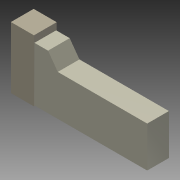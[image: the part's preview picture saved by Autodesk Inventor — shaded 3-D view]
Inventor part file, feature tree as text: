
AUTODESK INVENTOR PART (.ipt)
format: ipt  version: 2011 (Build 150239000, 239)  size: 106,496 bytes
history: native  units: in
note: dims shown in document units (in); Inventor stores cm internally (conversion verified against a paired STEP export)
features: extrude x4, sketch x4
ambient origin geometry x8: Origin, YZ Plane, XZ Plane, XY Plane, X Axis, Y Axis, Z Axis, Center Point
bodies: Solid1 (feature_tree)
feature tree (8):
  extrude  "Extrusion1"  Depth=0.425in
  extrude  "Extrusion2"  Depth=0.75in
  extrude  "Extrusion3"  Depth=0.25in
  extrude  "Extrusion4"  Depth=0.01in TaperAngle=0.0deg
  sketch  "Sketch1"  dims[d0=1.125in d1=0.425in]
  sketch  "Sketch2"  dims[d2=1.0in d3=0.75in]
  sketch  "Sketch3"  dims[d4=1.65in d5=0.25in]
  sketch  "Sketch4"  dims[d6=0.4in d7=0.0in d8=0.01in d9=0.0in d10=0.01in d11=0.0in d12=0.01in d13=0.0in]
